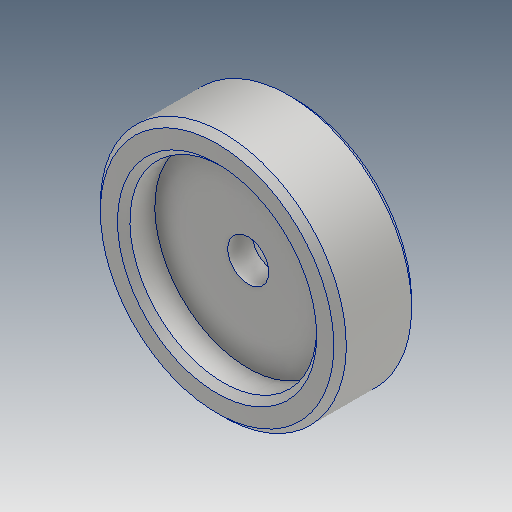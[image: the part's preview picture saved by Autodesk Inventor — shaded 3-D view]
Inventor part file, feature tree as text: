
AUTODESK INVENTOR PART (.ipt)
format: ipt  version: 2018.2 (Build 222227000, 227)  size: 156,672 bytes
history: native  units: mm
features: sketch x2, other x1, hole x1, chamfer x1
ambient origin geometry x8: Origin, YZ Plane, XZ Plane, XY Plane, X Axis, Y Axis, Z Axis, Center Point
bodies: Volumenkörper1 (feature_tree)
feature tree (5):
  other  "Grundkoerper"
  hole  "BOH_M6_ISO10642"  [1 undecoded]
  chamfer  "Fase1"  Distance=5.0mm
  sketch  "Skizze1"  dims[d0=12.5mm d1=39.5mm]
  sketch  "Skizze2"  dims[d2=30.0mm d3=5.0mm d4=90.0deg d5=6.6mm d6=6.0mm d7=13.7mm d8=2.0mm d9=90.0deg d10=8.0mm d11=20.594885mm d12=1.0mm d13=2.0mm d14=45.0deg]
note: 1 required parameter value undecoded (feature->parameter linkage not recoverable at this tier; creation-order binding heuristic only, values carry confidence <= 0.55)
